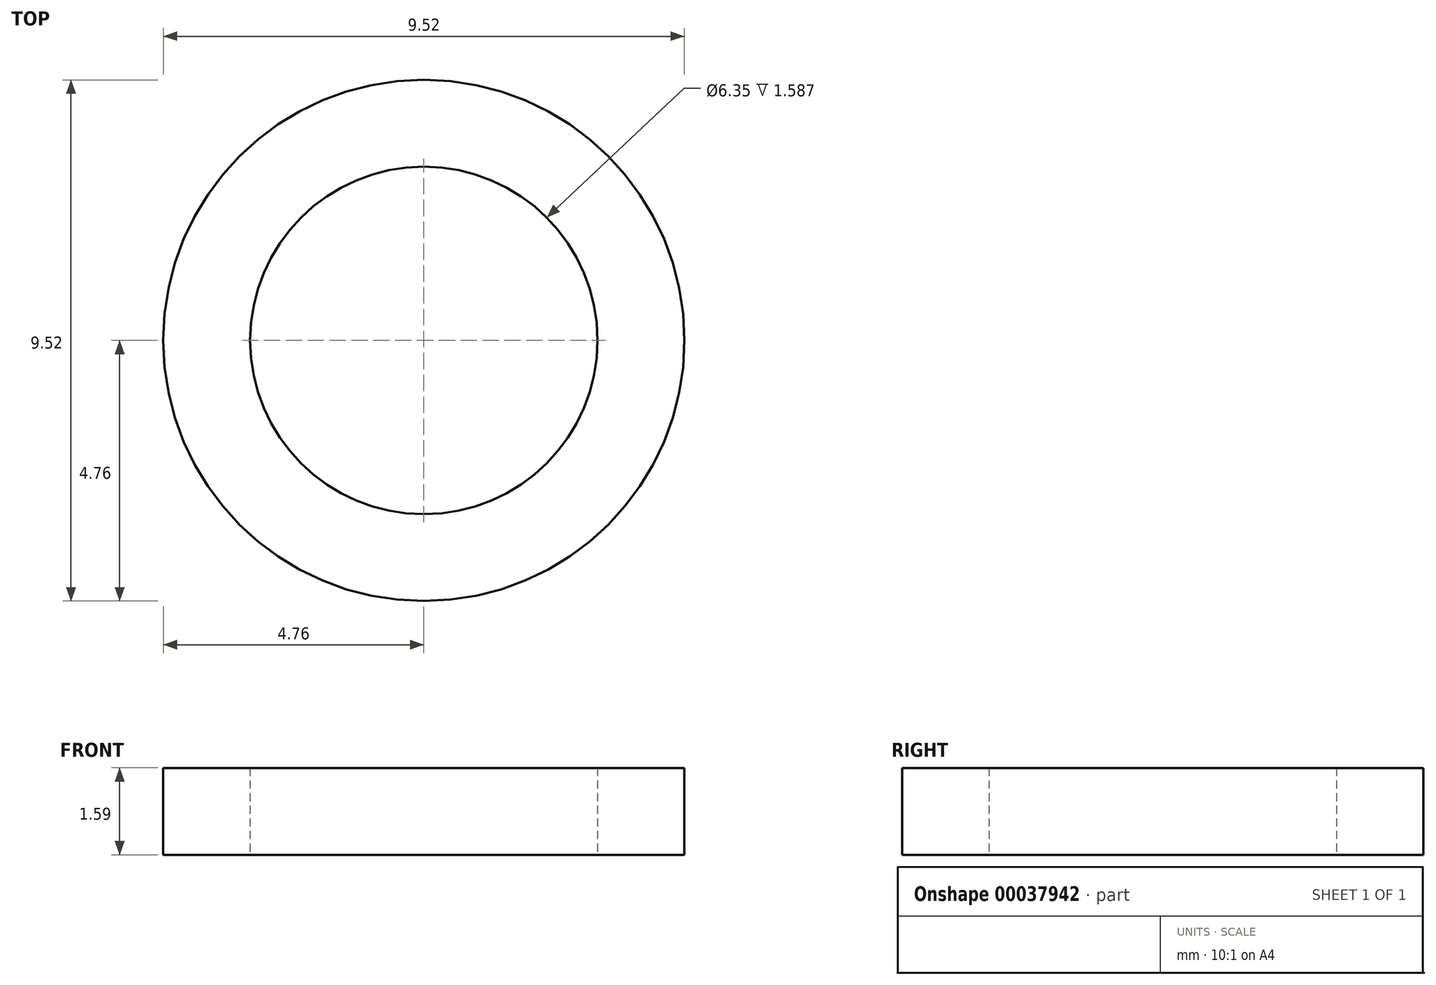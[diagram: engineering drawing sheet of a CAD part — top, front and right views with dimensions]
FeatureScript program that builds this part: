
annotation { "Feature Type Name" : "Feature", "Feature Type Description" : "" }
export const myFeature = defineFeature(function(context is Context, id is Id, definition is map)
    precondition{}
    {
        {
            var Q0;
            Q0=qCreatedBy(makeId("Top.planeOp"),FACE);
            var sketch = newSketch(context, id + "F0", { "sketchPlane" : qUnion([Q0])});
            skCircle(sketch, "E0", {"center": v(0, 0) * mm, "radius": 4.76 * mm});
            skCircle(sketch, "E1", {"center": v(0, 0) * mm, "radius": 3.18 * mm});
            skSolve(sketch);
        }
        {
            var Q0;
            Q0 = qSketchRegion(id + "F0", true);
            extrude(context, id + "F1", {"entities" : qUnion([Q0]), "depth" : 1.59 * mm});
        }
    });
